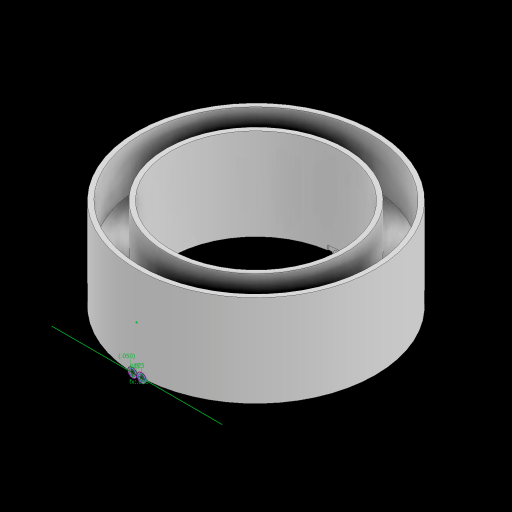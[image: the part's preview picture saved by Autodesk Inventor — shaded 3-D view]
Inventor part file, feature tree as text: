
AUTODESK INVENTOR PART (.ipt)
format: ipt  version: 2023 (Build 270158000, 158)  size: 239,104 bytes
history: native  units: in
note: dims shown in document units (in); Inventor stores cm internally (conversion verified against a paired STEP export)
features: extrude x5, sketch x5, plane x1
ambient origin geometry x8: Origin, YZ Plane, XZ Plane, XY Plane, X Axis, Y Axis, Z Axis, Center Point
bodies: Body1 (feature_tree)
feature tree (11):
  extrude  "Extrusion2"  Depth=1.25in
  extrude  "Extrusion3"  Depth=1.1875in
  plane  "Work Plane1"
  sketch  "Sketch3"  dims[d8=0.93in d9=1.3in]
  extrude  "Extrusion4"  Depth=1.3in
  extrude  "Extrusion5"  Depth=0.25in TaperAngle=0.0deg
  sketch  "Sketch4"  dims[d10=0.25in d11=0.0in d12=0.25in d13=0.0in]
  extrude  "Extrusion7"  Depth=0.064in
  sketch  "Sketch1"  dims[d2=0.98in d3=1.25in]
  sketch  "Sketch2"  dims[d6=1.0in d7=1.1875in]
  sketch  "Sketch5"  dims[d14=0.025in d15=0.05in d16=0.025in d17=0.05in d18=1.3in d19=0.0in d20=1.3in d21=0.0in d22=0.0638in d23=0.0638in d24=0.0in d25=0.15in d26=0.15in d27=0.15in d28=0.15in d29=0.064in d30=0.064in d33=0.0in d34=0.15in d35=0.15in d36=0.15in d37=0.15in d38=0.064in d39=0.064in d40=0.05in d41=0.0in d42=0.5in d43=0.0344in]
